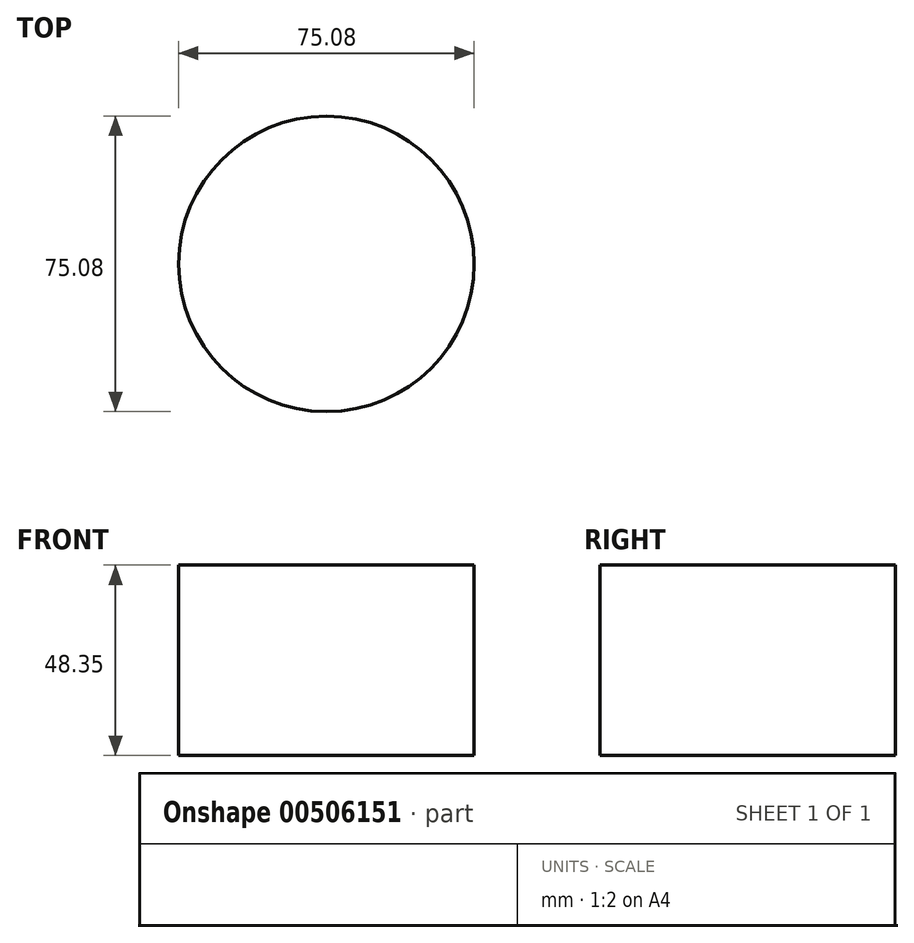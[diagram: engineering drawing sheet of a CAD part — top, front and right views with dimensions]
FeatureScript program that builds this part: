
annotation { "Feature Type Name" : "Feature", "Feature Type Description" : "" }
export const myFeature = defineFeature(function(context is Context, id is Id, definition is map)
    precondition{}
    {
        {
            var Q0;
            Q0=qCreatedBy(makeId("Front.planeOp"),FACE);
            var sketch = newSketch(context, id + "F0", { "sketchPlane" : qUnion([Q0])});
            skLineSegment(sketch, "E0.bottom", {"start": v(-83.87, 52.92) * mm, "end": v(-46.33, 52.92) * mm});
            skLineSegment(sketch, "E0.top", {"start": v(-83.87, 4.57) * mm, "end": v(-46.33, 4.57) * mm});
            skLineSegment(sketch, "E0.left", {"start": v(-83.87, 52.92) * mm, "end": v(-83.87, 4.57) * mm});
            skLineSegment(sketch, "E0.right", {"start": v(-46.33, 52.92) * mm, "end": v(-46.33, 4.57) * mm});
            skSolve(sketch);
        }
        {
            var Q0;
            Q0=makeQuery(id+"F0.imprint","IMPRINT",FACE,{"disambiguationData":[TD([[makeQuery(id+"F0.imprint","IMPRINT",EDGE,{"derivedFrom":sQuery(id+"F0.wireOp",EDGE,"E0.bottom")}),-1.0]])]});
            var Q1;
            Q1=sQuery(id+"F0.wireOp",EDGE,"E0.right");
            revolve(context, id + "F1", {"entities" : qUnion([Q0]), "axis" : qUnion([Q1]), "revolveType" : RevolveType.FULL});
        }
    });
